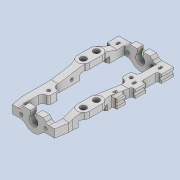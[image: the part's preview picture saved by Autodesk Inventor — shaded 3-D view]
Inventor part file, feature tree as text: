
AUTODESK INVENTOR PART (.ipt)
format: ipt  version: 2020 (Build 240168000, 168)  size: 1,101,824 bytes
history: native  units: mm
features: projected_geometry x34, sketch x30, extrude x28, thicken_offset x10, fillet x10, chamfer x7, other x5, plane x3, reference x3, hole x2
ambient origin geometry x8: Origin, YZ Plane, XZ Plane, XY Plane, X Axis, Y Axis, Z Axis, Center Point
bodies: Solid1 (feature_tree)
feature tree (132):
  extrude  "Extrusion1"  Depth=10.0mm
  plane  "Work Plane1"
  extrude  "Extrusion2"  Depth=2.0mm TaperAngle=0.0deg
  extrude  "Extrusion3"  Depth=10.0mm
  extrude  "Extrusion4"  Depth=2.0mm TaperAngle=0.0deg
  hole  "Hole1"  [1 undecoded]
  thicken_offset  "Thicken1"
  thicken_offset  "Thicken2"
  thicken_offset  "Thicken3"
  thicken_offset  "Thicken4"
  extrude  "Extrusion5"  Depth=54.0mm
  extrude  "Extrusion6"  Depth=4.5mm
  extrude  "Extrusion8"  Depth=6.0mm
  extrude  "Extrusion9"  Depth=3.5mm
  extrude  "Extrusion11"  Depth=3.5mm
  hole  "Hole2"  [1 undecoded]
  extrude  "Extrusion15"  Depth=3.5mm
  extrude  "Extrusion16"  Depth=7.5mm
  chamfer  "Chamfer1"  Distance=2.0mm
  chamfer  "Chamfer2"  Distance=2.0mm
  chamfer  "Chamfer3"  Distance=3.0mm
  chamfer  "Chamfer4"  Distance=3.0mm
  fillet  "Fillet4"  Radius=3.0mm
  fillet  "Fillet5"  Radius=3.0mm
  chamfer  "Chamfer5"  Distance=6.5mm
  fillet  "Fillet6"  Radius=7.0mm
  extrude  "Extrusion17"  Depth=1.0mm TaperAngle=0.0deg
  plane  "Work Plane3"
  extrude  "Extrusion18"  Depth=1.0mm
  plane  "Work Plane4"
  extrude  "Extrusion19"  Depth=1.0mm TaperAngle=0.0deg
  extrude  "Extrusion20"  Depth=1.0mm
  extrude  "Extrusion21"  Depth=1.0mm TaperAngle=0.0deg
  extrude  "Extrusion22"  Depth=1.0mm TaperAngle=30.0deg
  thicken_offset  "Thicken9"
  thicken_offset  "Thicken10"
  thicken_offset  "Thicken11"
  thicken_offset  "Thicken12"
  extrude  "Extrusion23"  Depth=1.0mm TaperAngle=30.0deg
  fillet  "Fillet11"  Radius=12.0mm
  extrude  "Extrusion24"  Depth=1.0mm TaperAngle=30.0deg
  thicken_offset  "Thicken13"
  thicken_offset  "Thicken14"
  chamfer  "Chamfer7"  Distance=1.0mm
  chamfer  "Chamfer8"  Distance=8.0mm
  fillet  "Fillet12"  Radius=1.0mm
  fillet  "Fillet13"  Radius=0.5mm
  fillet  "Fillet14"  Radius=2.5mm
  extrude  "Extrusion26"  Depth=1.0mm
  extrude  "Extrusion27"  Depth=1.0mm
  extrude  "Extrusion28"  Depth=1.0mm TaperAngle=0.0deg
  extrude  "Extrusion29"  Depth=1.0mm
  fillet  "Fillet15"  Radius=5.0mm
  fillet  "Fillet16"  Radius=9.0mm
  extrude  "Extrusion30"  Depth=1.0mm TaperAngle=0.0deg
  extrude  "Extrusion31"  Depth=1.0mm
  extrude  "Extrusion32"  Depth=1.0mm
  extrude  "Extrusion33"  Depth=1.0mm
  extrude  "Extrusion34"  Depth=1.0mm TaperAngle=0.0deg
  fillet  "Fillet17"  Radius=3.0mm
  sketch  "Sketch1"  dims[d0=10.0mm d1=4.0mm]
  sketch  "Sketch2"  dims[d2=30.0mm d3=2.0mm d4=0.0mm]
  sketch  "Sketch3"  dims[d5=10.0mm d6=4.0mm]
  projected_geometry  "Projected Loop1"
  projected_geometry  "Projected Loop2"
  projected_geometry  "Projected Loop3"
  projected_geometry  "Projected Loop4"
  sketch  "Sketch4"  dims[d7=30.0mm d8=2.0mm d9=0.0mm]
  sketch  "Sketch5"  dims[d10=3.0mm d11=54.0mm]
  sketch  "Sketch6"  dims[d12=3.0mm d13=54.0mm]
  projected_geometry  "Projected Loop5"
  reference  "Reference1"
  reference  "Reference2"
  sketch  "Sketch7"  dims[d14=2.0mm d15=0.0mm d16=4.5mm]
  projected_geometry  "Projected Loop6"
  reference  "Reference3"
  sketch  "Sketch9"  dims[d17=2.0mm d18=0.0mm d19=6.0mm]
  projected_geometry  "Projected Loop9"
  sketch  "Sketch10"  dims[d20=6.0mm]
  projected_geometry  "Projected Loop10"
  sketch  "Sketch12"  dims[d21=1.6mm d22=6.0mm d23=4.0mm d24=2.0mm d25=90.0deg d26=100.0mm d27=0.0mm d28=3.5mm]
  projected_geometry  "Projected Loop13"
  sketch  "Sketch13"  dims[d29=3.5mm d30=3.5mm]
  projected_geometry  "Projected Loop14"
  sketch  "Sketch18"  dims[d31=3.5mm d32=3.5mm]
  projected_geometry  "Projected Loop20"
  sketch  "Sketch19"  dims[d33=3.5mm d34=3.5mm]
  projected_geometry  "Projected Loop21"
  sketch  "Sketch20"  dims[d35=3.5mm d36=7.5mm]
  projected_geometry  "Projected Loop22"
  sketch  "Sketch21"  dims[d37=9.0mm]
  projected_geometry  "Projected Loop23"
  sketch  "Sketch22"  dims[d38=3.0mm]
  projected_geometry  "Projected Loop24"
  sketch  "Sketch23"  dims[d39=3.25mm]
  projected_geometry  "Projected Loop25"
  sketch  "Sketch24"  dims[d40=3.25mm]
  projected_geometry  "Projected Loop26"
  sketch  "Sketch25"  dims[d41=6.0mm]
  projected_geometry  "Projected Loop27"
  sketch  "Sketch26"  dims[d42=6.0mm]
  projected_geometry  "Projected Loop28"
  projected_geometry  "Projected Loop29"
  sketch  "Sketch27"  dims[d43=2.0mm]
  projected_geometry  "Projected Loop30"
  projected_geometry  "Projected Loop31"
  sketch  "Sketch29"  dims[d44=6.5mm]
  projected_geometry  "Projected Loop33"
  sketch  "Sketch30"  dims[d45=6.0mm d46=2.0mm d47=0.0mm]
  projected_geometry  "Projected Loop34"
  projected_geometry  "Projected Loop35"
  sketch  "Sketch31"  dims[d48=7.5mm]
  projected_geometry  "Projected Loop36"
  sketch  "Sketch32"  dims[d49=9.0mm]
  projected_geometry  "Projected Loop37"
  projected_geometry  "Projected Loop38"
  sketch  "Sketch34"  dims[d50=2.0mm]
  projected_geometry  "Projected Loop40"
  sketch  "Sketch35"  dims[d51=3.25mm]
  projected_geometry  "Projected Loop41"
  sketch  "Sketch36"  dims[d52=6.5mm]
  projected_geometry  "Projected Loop42"
  sketch  "Sketch37"  dims[d53=6.0mm d54=2.0mm d55=0.0mm]
  projected_geometry  "Projected Loop43"
  projected_geometry  "Projected Loop44"
  sketch  "Sketch38"  dims[d60=7.0mm d61=3.0mm d62=0.0mm d66=3.0mm d67=3.0mm d68=3.0mm d69=0.0mm d76=6.5mm d77=7.0mm d78=3.0mm d79=0.0mm d80=3.0mm d81=6.0mm d82=4.0mm d83=2.0mm d84=90.0deg d85=100.0mm d86=0.0mm d107=6.0mm d108=2.0mm d109=0.0mm d110=6.0mm d111=2.0mm d112=0.0mm d113=12.0mm d114=2.0mm d115=30.0deg d116=5.0mm d117=2.0mm d118=30.0deg d119=12.0mm d120=2.0mm d121=30.0deg d122=5.0mm d123=2.0mm d124=30.0deg d125=1.0mm d126=8.0mm d127=1.0mm d128=2.0mm d129=30.0deg d130=0.5mm d135=2.5mm d136=2.0mm d137=4.0mm d138=5.0mm d139=0.0mm d140=8.0mm d141=5.0mm d142=0.0mm d143=9.0mm d144=4.0mm d145=0.0mm d146=2.5mm d147=2.0mm d148=4.0mm d149=5.0mm d150=0.0mm d154=3.0mm d155=2.0mm d156=3.0mm d157=2.0mm d158=3.0mm d159=2.0mm d160=0.5mm d161=1.0mm d162=0.5mm d163=1.0mm d164=0.5mm d165=1.0mm d166=8.0mm d167=0.0mm d168=3.0mm d169=0.5mm d170=1.0mm d171=8.0mm d172=0.0mm d173=0.5mm d174=0.5mm d175=0.5mm d176=0.5mm d177=0.5mm d178=0.5mm d179=0.5mm d180=0.5mm d181=12.0mm d182=1.5mm d183=3.0mm d184=5.0mm d185=12.0mm d186=1.5mm d187=3.0mm d188=5.0mm d189=8.0mm d190=0.0mm d191=2.0mm d192=2.5mm d193=1.6mm d194=2.5mm d195=1.6mm d196=8.0mm d197=0.0mm d198=1.0mm d199=1.0mm d200=1.0mm d201=1.0mm d202=1.0mm d203=6.0mm d204=30.0deg d205=1.0mm d206=6.0mm d207=30.0deg d208=4.0mm d209=4.0mm d210=1.0mm d215=6.0mm d216=3.0mm d217=10.0mm d218=0.0mm d219=10.0mm d220=0.0mm d221=2.0mm d222=2.0mm d223=10.0mm d224=0.0mm d225=10.0mm d226=0.0mm d227=2.0mm d228=3.0mm d230=2.0mm d231=0.25mm d232=1.5mm d233=10.0mm d234=0.0mm d235=1.5mm d236=10.0mm d237=0.0mm d238=10.0mm d239=0.0mm d240=10.0mm d241=0.0mm d242=1.5mm d243=10.0mm d244=0.0mm d245=1.0mm]
  projected_geometry  "Projected Loop45"
  parser-record x1  (decoder bookkeeping rows leaked as tree rows — omitted from the tree; the rows remain in map.json)
  other  "tip2_ass_t1.iam"
  other  "cab_coil_1:1"
  other  "cab_coil_1:2"
  other  "bearing_3_6_2:1"
note: 2 required parameter values undecoded (feature->parameter linkage not recoverable at this tier; creation-order binding heuristic only, values carry confidence <= 0.55)
note: 1 file-system path scrubbed to <path> (originals preserved in map.json)
